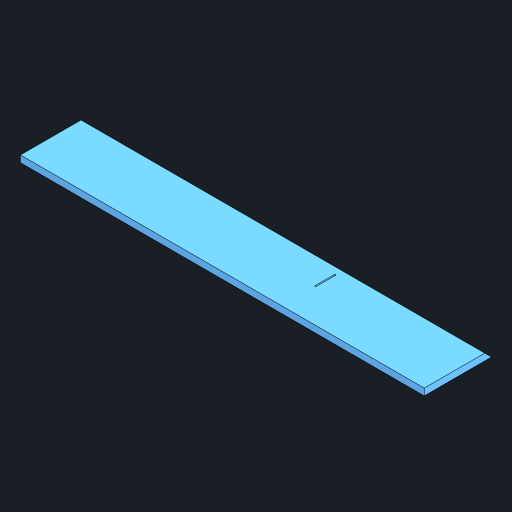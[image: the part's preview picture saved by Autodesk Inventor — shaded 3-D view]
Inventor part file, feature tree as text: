
AUTODESK INVENTOR PART (.ipt)
format: ipt  version: 2023 (Build 270158000, 158)  size: 122,880 bytes
history: native  units: mm
features: extrude x2, other x1, chamfer x1, sketch x1
ambient origin geometry x8: Origin, YZ Plane, XZ Plane, XY Plane, X Axis, Y Axis, Z Axis, Center Point
bodies: Body1 (feature_tree)
feature tree (5):
  other  "ソリッド1"
  extrude  "押し出し1"  Depth=300.0mm
  chamfer  "面取り1"  Distance=50.0mm
  extrude  "押し出し4"  Depth=5.0mm TaperAngle=0.0deg
  sketch  "スケッチ4"
